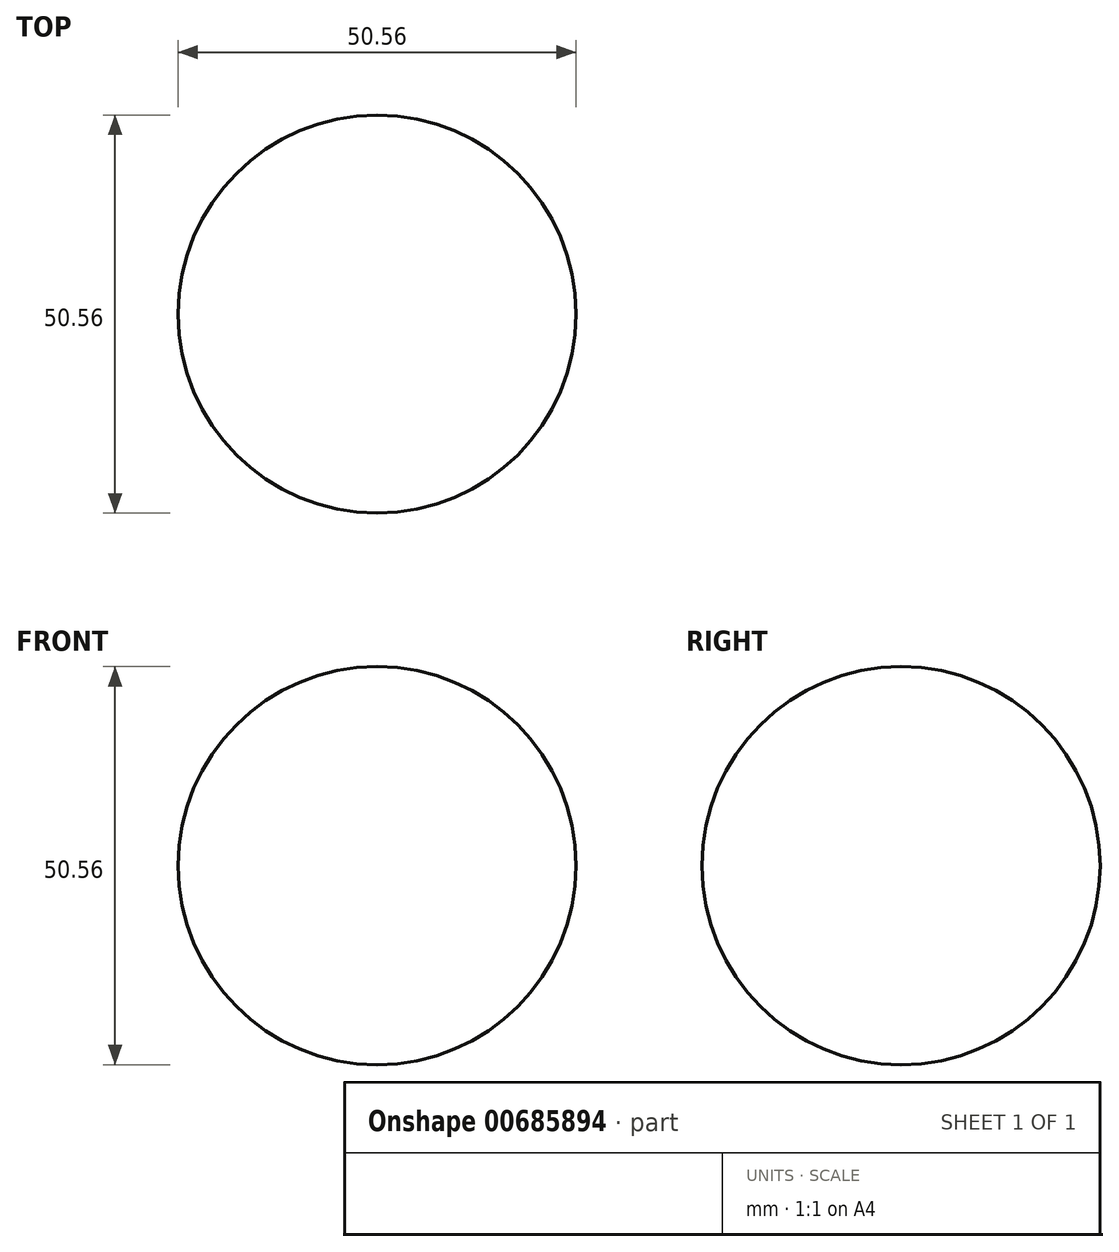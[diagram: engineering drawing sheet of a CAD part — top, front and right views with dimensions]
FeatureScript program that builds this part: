
annotation { "Feature Type Name" : "Feature", "Feature Type Description" : "" }
export const myFeature = defineFeature(function(context is Context, id is Id, definition is map)
    precondition{}
    {
        {
            var Q0;
            Q0=qCreatedBy(makeId("Top.planeOp"),FACE);
            var sketch = newSketch(context, id + "F0", { "sketchPlane" : qUnion([Q0])});
            skArc(sketch, "E0", {"start": v(0, 25.28) * mm, "mid": v(-25.28, 0) * mm, "end": v(0, -25.28) * mm});
            skLineSegment(sketch, "E1", {"start": v(0, 0) * mm, "end": v(0, 41.15) * mm});
            skLineSegment(sketch, "E2", {"start": v(0, 0) * mm, "end": v(0, -36.19) * mm});
            skSolve(sketch);
        }
        {
            var Q0;
            {var subQ0=sQuery(id+"F0.wireOp",EDGE,"E0");Q0=makeQuery(id+"F0.imprint","IMPRINT",FACE,{"disambiguationData":[TD([[makeQuery(id+"F0.imprint","IMPRINT",EDGE,{"derivedFrom":subQ0}),1.0]])]});}
            var Q1;
            Q1=sQuery(id+"F0.wireOp",EDGE,"E1");
            revolve(context, id + "F1", {"entities" : qUnion([Q0]), "axis" : qUnion([Q1]), "revolveType" : RevolveType.FULL});
        }
    });
